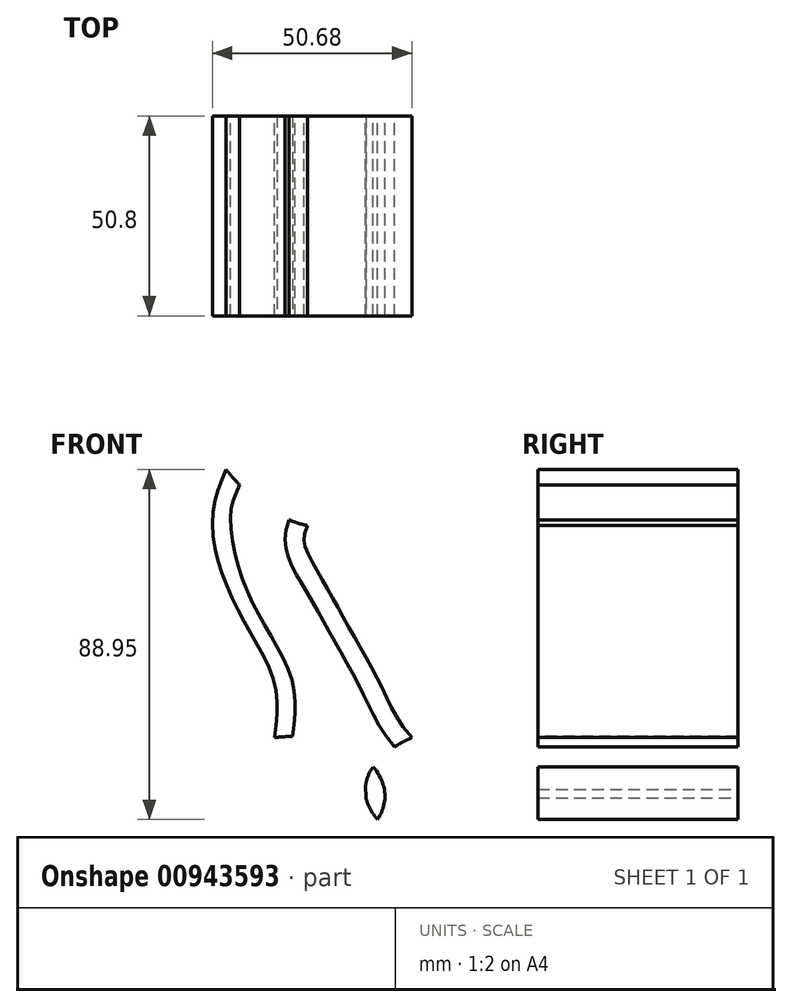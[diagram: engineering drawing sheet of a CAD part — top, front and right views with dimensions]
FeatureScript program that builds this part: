
annotation { "Feature Type Name" : "Feature", "Feature Type Description" : "" }
export const myFeature = defineFeature(function(context is Context, id is Id, definition is map)
    precondition{}
    {
        {
            var Q0;
            Q0=qCreatedBy(makeId("Front.planeOp"),FACE);
            var sketch = newSketch(context, id + "F0", { "sketchPlane" : qUnion([Q0])});
            skEllipse(sketch, "E0", {"center": v(-24.37, 10.92) * mm, "majorRadius": 23.51 * mm, "minorRadius": 15.19 * mm, "majorAxis": v(1, 0)});
            skEllipse(sketch, "E1", {"center": v(-24.37, 10.92) * mm, "majorRadius": 18.72 * mm, "minorRadius": 12.1 * mm, "majorAxis": v(1, 0)});
            skEllipse(sketch, "E2", {"center": v(27.08, 12.43) * mm, "majorRadius": 32.94 * mm, "minorRadius": 17.44 * mm, "majorAxis": v(1, 0)});
            skFitSpline(sketch, "E3", {"points": [v(-28.9, 25.82) * mm, v(-28.8, 39.18) * mm, v(-35.33, 52.96) * mm, v(-42.4, 68) * mm, v(-44.57, 82.87) * mm, v(-41.13, 94.1) * mm], "startDerivative": vector(8.44, 70.1) * mm, "endDerivative": vector(25.17, 59.33) * mm});
            skFitSpline(sketch, "E4", {"points": [v(6, 25.82) * mm, v(-1.98, 39.18) * mm, v(-9.4, 52.78) * mm, v(-16.11, 64.74) * mm, v(-21, 73.99) * mm, v(-20.5, 79.72) * mm], "startDerivative": vector(-57.3, 66.34) * mm, "endDerivative": vector(25.17, 59.33) * mm});
            skFitSpline(sketch, "E5", {"points": [v(-24.31, 26.1) * mm, v(-24.22, 39.47) * mm, v(-30.75, 53.24) * mm, v(-37.82, 68.29) * mm, v(-40, 83.15) * mm, v(-37.68, 90.31) * mm], "startDerivative": vector(8.44, 70.1) * mm, "endDerivative": vector(25.17, 59.33) * mm});
            skFitSpline(sketch, "E6", {"points": [v(1.63, 23.5) * mm, v(-6.34, 36.86) * mm, v(-13.77, 50.45) * mm, v(-20.48, 62.41) * mm, v(-25.37, 71.66) * mm, v(-25.17, 81.25) * mm], "startDerivative": vector(-57.3, 66.34) * mm, "endDerivative": vector(25.17, 59.33) * mm});
            skFitSpline(sketch, "E7", {"points": [v(-43.52, 104.01) * mm, v(-32.7, 85.66) * mm, v(-13.45, 81.52) * mm, v(-8.54, 105.9) * mm, v(-15.85, 110.92) * mm, v(-43.52, 104.01) * mm]});
            skPoint(sketch, "E8", {"position": v(27.08, 29.86) * mm});
            skFitSpline(sketch, "E9.0", {"points": [v(52, 12.2) * mm, v(52.03, 12.43) * mm, v(52, 12.66) * mm, v(51.92, 12.99) * mm, v(51.7, 13.48) * mm, v(51.26, 14.15) * mm, v(50.56, 14.94) * mm, v(49.56, 15.83) * mm, v(48.49, 16.6) * mm, v(47.47, 17.22) * mm, v(46.64, 17.69) * mm, v(45.74, 18.14) * mm, v(44.46, 18.72) * mm, v(42.73, 19.4) * mm, v(40.45, 20.13) * mm, v(38, 20.74) * mm, v(35.4, 21.23) * mm, v(32.71, 21.6) * mm, v(30.4, 21.77) * mm, v(28.5, 21.85) * mm, v(27.08, 21.87) * mm, v(25.66, 21.85) * mm, v(23.77, 21.77) * mm, v(21.45, 21.6) * mm, v(18.76, 21.23) * mm, v(16.17, 20.74) * mm, v(13.72, 20.13) * mm, v(11.44, 19.4) * mm, v(9.7, 18.72) * mm, v(8.42, 18.14) * mm, v(7.52, 17.69) * mm, v(6.69, 17.22) * mm, v(5.68, 16.6) * mm, v(4.6, 15.83) * mm, v(3.6, 14.94) * mm, v(2.9, 14.15) * mm, v(2.47, 13.48) * mm, v(2.24, 12.99) * mm, v(2.16, 12.66) * mm, v(2.14, 12.43) * mm, v(2.16, 12.2) * mm, v(2.24, 11.86) * mm, v(2.47, 11.37) * mm, v(2.9, 10.7) * mm, v(3.6, 9.9) * mm, v(4.6, 9.02) * mm, v(5.68, 8.25) * mm, v(6.69, 7.63) * mm, v(7.52, 7.16) * mm, v(8.42, 6.71) * mm, v(9.7, 6.13) * mm, v(11.44, 5.45) * mm, v(13.72, 4.72) * mm, v(16.17, 4.1) * mm, v(18.76, 3.62) * mm, v(21.45, 3.26) * mm, v(23.77, 3.08) * mm, v(25.66, 3) * mm, v(27.08, 2.98) * mm, v(28.5, 3) * mm, v(30.4, 3.08) * mm, v(32.71, 3.26) * mm, v(35.4, 3.62) * mm, v(38, 4.1) * mm, v(40.45, 4.72) * mm, v(42.73, 5.45) * mm, v(44.46, 6.13) * mm, v(45.74, 6.71) * mm, v(46.64, 7.16) * mm, v(47.47, 7.63) * mm, v(48.49, 8.25) * mm, v(49.56, 9.02) * mm, v(50.56, 9.9) * mm, v(51.26, 10.7) * mm, v(51.7, 11.37) * mm, v(51.92, 11.86) * mm, v(52, 12.2) * mm, v(52.03, 12.43) * mm, v(52, 12.66) * mm, v(52, 12.2) * mm]});
            skLineSegment(sketch, "E10.bottom", {"start": v(5.2, 107.74) * mm, "end": v(43.47, 43.23) * mm});
            skLineSegment(sketch, "E10.top", {"start": v(-3, 97.06) * mm, "end": v(30.17, 41.16) * mm});
            skLineSegment(sketch, "E10.left", {"start": v(5.2, 107.74) * mm, "end": v(-1.24, 103.91) * mm});
            skLineSegment(sketch, "E10.right", {"start": v(43.47, 43.23) * mm, "end": v(37.02, 39.4) * mm});
            skPoint(sketch, "E11.visualSharp", {"position": v(32.72, 36.86) * mm});
            skArc(sketch, "E11.filletArc", {"start": v(30.17, 41.16) * mm, "mid": v(33.24, 38.86) * mm, "end": v(37.02, 39.4) * mm});
            skPoint(sketch, "E12.visualSharp", {"position": v(-5.54, 101.36) * mm});
            skArc(sketch, "E12.filletArc", {"start": v(-1.24, 103.91) * mm, "mid": v(-3.54, 100.85) * mm, "end": v(-3, 97.06) * mm});
            skSolve(sketch);
        }
        {
            var Q0;
            Q0=makeQuery(id+"F0.imprint","IMPRINT",FACE,{"disambiguationData":[TD([[makeQuery(id+"F0.imprint","IMPRINT",EDGE,{"derivedFrom":sQuery(id+"F0.wireOp",EDGE,"oqUmaDUs-UD67-WHlT-hdRB-88egpidpviUN")}),-1.0]])]});
            var Q1;
            {var subQ0=sQuery(id+"F0.wireOp",EDGE,"E4");Q1=makeQuery(id+"F0.imprint","IMPRINT",FACE,{"disambiguationData":[TD([[makeQuery(id+"F0.imprint","IMPRINT",EDGE,{"derivedFrom":subQ0}),1.0]])]});}
            var Q2;
            Q2=makeQuery(id+"F0.imprint","IMPRINT",FACE,{"disambiguationData":[TD([[makeQuery(id+"F0.imprint","IMPRINT",EDGE,{"derivedFrom":sQuery(id+"F0.wireOp",EDGE,"627b5b5b-95c3-461e-bb4c-25a893bf08c0.0")}),-1.0]])]});
            var Q3;
            {var subQ0=sQuery(id+"F0.wireOp",EDGE,"E3");var subQ1=sQuery(id+"F0.wireOp",EDGE,"E0");var subQ2=makeQuery(id+"F0.imprint","INTERSECT",VERTEX,{"derivedFrom":[subQ1,subQ0]});Q3=makeQuery(id+"F0.imprint","IMPRINT",FACE,{"disambiguationData":[TD([[makeQuery(id+"F0.imprint","IMPRINT",EDGE,{"disambiguationData":[TD([[subQ2,1.0]])],"derivedFrom":subQ1}),-1.0]])]});}
            var Q4;
            {var subQ0=sQuery(id+"F0.wireOp",EDGE,"E2");var subQ1=sQuery(id+"F0.wireOp",EDGE,"E0");var subQ2=makeQuery(id+"F0.imprint","INTERSECT",VERTEX,{"disambiguationData":[OD(0.0)],"derivedFrom":[subQ1,subQ0]});Q4=makeQuery(id+"F0.imprint","IMPRINT",FACE,{"disambiguationData":[TD([[makeQuery(id+"F0.imprint","IMPRINT",EDGE,{"disambiguationData":[TD([[subQ2,-1.0]])],"derivedFrom":subQ1}),1.0]])]});}
            var Q5;
            Q5=makeQuery(id+"F0.imprint","IMPRINT",FACE,{"disambiguationData":[TD([[makeQuery(id+"F0.imprint","IMPRINT",EDGE,{"derivedFrom":sQuery(id+"F0.wireOp",EDGE,"E1")}),-1.0]])]});
            extrude(context, id + "F1", {"entities" : qUnion([Q0, Q1, Q2, Q3, Q4, Q5]), "depth" : 50.8 * mm, "offsetDistance" : 25.4 * mm});
        }
    });
